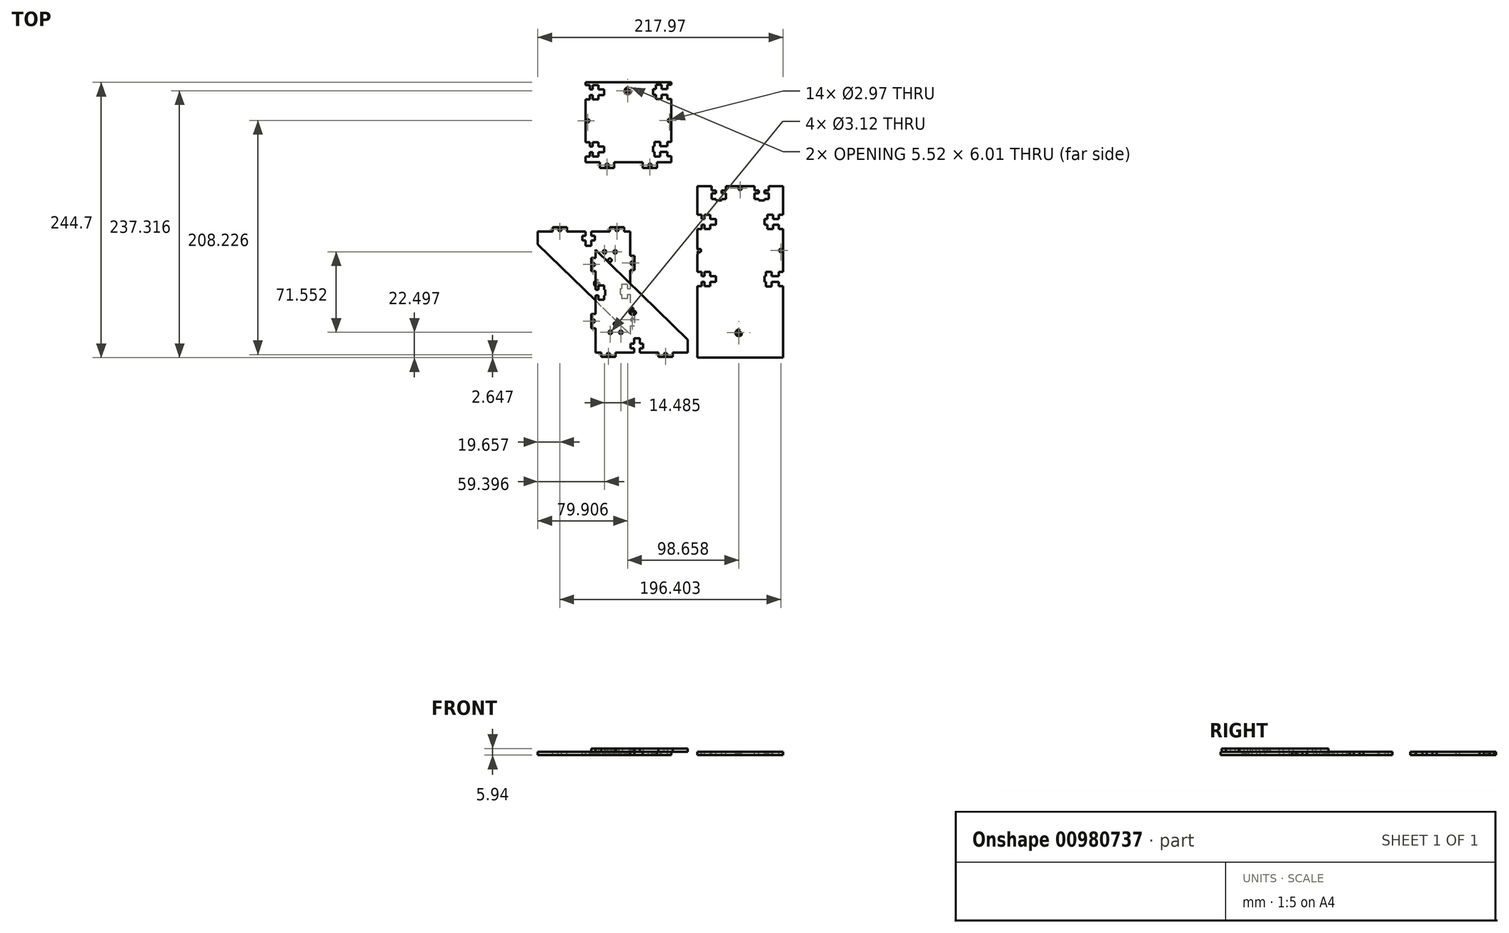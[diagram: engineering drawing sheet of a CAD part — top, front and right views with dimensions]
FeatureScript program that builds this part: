
annotation { "Feature Type Name" : "Feature", "Feature Type Description" : "" }
export const myFeature = defineFeature(function(context is Context, id is Id, definition is map)
    precondition{}
    {
        {
            var Q0;
            Q0=qCreatedBy(makeId("Top.planeOp"),FACE);
            var sketch = newSketch(context, id + "F0", { "sketchPlane" : qUnion([Q0])});
            skLineSegment(sketch, "E0.bottom", {"start": v(-31.04, 87.19) * mm, "end": v(45.16, 87.19) * mm});
            skLineSegment(sketch, "E0.top", {"start": v(-31.04, -65.21) * mm, "end": v(45.16, -65.21) * mm});
            skLineSegment(sketch, "E0.left", {"start": v(-31.04, 87.19) * mm, "end": v(-31.04, -65.21) * mm});
            skLineSegment(sketch, "E0.right", {"start": v(45.16, 87.19) * mm, "end": v(45.16, -65.21) * mm});
            skSolve(sketch);
        }
        {
            var Q0;
            Q0=qSketchRegion(id+"F0",true);
            extrude(context, id + "F1", {"entities" : qUnion([Q0]), "depth" : 2.97 * mm, "offsetDistance" : 25.4 * mm});
        }
        {
            var Q0;
            Q0=makeQuery(id+"F1.opExtrude","CAP_FACE",FACE,{"disambiguationData":[OSD([sQuery(id+"F0.wireOp",EDGE,"E0.bottom"),sQuery(id+"F0.wireOp",EDGE,"E0.top"),sQuery(id+"F0.wireOp",EDGE,"E0.left"),sQuery(id+"F0.wireOp",EDGE,"E0.right")])],"isStart":false});
            var sketch = newSketch(context, id + "F2", { "sketchPlane" : qUnion([Q0])});
            skLineSegment(sketch, "E1.bottom", {"start": v(-31.04, 61.79) * mm, "end": v(-27.23, 61.79) * mm});
            skLineSegment(sketch, "E1.top", {"start": v(-31.04, 49.09) * mm, "end": v(-27.23, 49.09) * mm});
            skLineSegment(sketch, "E1.left", {"start": v(-31.04, 61.79) * mm, "end": v(-31.04, 49.09) * mm});
            skLineSegment(sketch, "E1.right", {"start": v(-27.23, 61.79) * mm, "end": v(-27.23, 49.09) * mm});
            skLineSegment(sketch, "E2", {"start": v(-24.7, 61.79) * mm, "end": v(-24.7, 87.19) * mm, "construction": true});
            skLineSegment(sketch, "E3", {"start": v(-31.04, 33.1) * mm, "end": v(-31.04, 33.1) * mm});
            skLineSegment(sketch, "E4.bottom", {"start": v(-14.53, 52.9) * mm, "end": v(-39.93, 52.9) * mm});
            skLineSegment(sketch, "E4.top", {"start": v(-14.53, 57.98) * mm, "end": v(-39.93, 57.98) * mm});
            skLineSegment(sketch, "E4.left", {"start": v(-14.53, 52.9) * mm, "end": v(-14.53, 57.98) * mm});
            skLineSegment(sketch, "E4.right", {"start": v(-39.93, 52.9) * mm, "end": v(-39.93, 57.98) * mm});
            skPoint(sketch, "E4.middle", {"position": v(-27.23, 55.44) * mm});
            skLineSegment(sketch, "E5.bottom", {"start": v(-24.7, 61.79) * mm, "end": v(-19.61, 61.79) * mm});
            skLineSegment(sketch, "E5.top", {"start": v(-24.7, 49.09) * mm, "end": v(-19.61, 49.09) * mm});
            skLineSegment(sketch, "E5.left", {"start": v(-24.7, 61.79) * mm, "end": v(-24.7, 49.09) * mm});
            skLineSegment(sketch, "E5.right", {"start": v(-19.61, 61.79) * mm, "end": v(-19.61, 49.09) * mm});
            skLineSegment(sketch, "E6.bottom", {"start": v(-31.04, 10.99) * mm, "end": v(-27.23, 10.99) * mm});
            skLineSegment(sketch, "E6.top", {"start": v(-31.04, -1.71) * mm, "end": v(-27.23, -1.71) * mm});
            skLineSegment(sketch, "E6.left", {"start": v(-31.04, 10.99) * mm, "end": v(-31.04, -1.71) * mm});
            skLineSegment(sketch, "E6.right", {"start": v(-27.23, 10.99) * mm, "end": v(-27.23, -1.71) * mm});
            skLineSegment(sketch, "E7", {"start": v(11.23, 8.06) * mm, "end": v(11.23, 8.06) * mm});
            skLineSegment(sketch, "E8.bottom", {"start": v(-14.53, 2.1) * mm, "end": v(-39.93, 2.1) * mm});
            skLineSegment(sketch, "E8.top", {"start": v(-14.53, 7.18) * mm, "end": v(-39.93, 7.18) * mm});
            skLineSegment(sketch, "E8.left", {"start": v(-14.53, 2.1) * mm, "end": v(-14.53, 7.18) * mm});
            skLineSegment(sketch, "E8.right", {"start": v(-39.93, 2.1) * mm, "end": v(-39.93, 7.18) * mm});
            skPoint(sketch, "E8.middle", {"position": v(-27.23, 4.64) * mm});
            skLineSegment(sketch, "E9.bottom", {"start": v(-24.7, 10.99) * mm, "end": v(-19.61, 10.99) * mm});
            skLineSegment(sketch, "E9.top", {"start": v(-24.7, -1.71) * mm, "end": v(-19.61, -1.71) * mm});
            skLineSegment(sketch, "E9.left", {"start": v(-24.7, 10.99) * mm, "end": v(-24.7, -1.71) * mm});
            skLineSegment(sketch, "E9.right", {"start": v(-19.61, 10.99) * mm, "end": v(-19.61, -1.71) * mm});
            skLineSegment(sketch, "E10.bottom", {"start": v(-18.34, 87.19) * mm, "end": v(-5.64, 87.19) * mm});
            skLineSegment(sketch, "E10.top", {"start": v(-18.34, 83.38) * mm, "end": v(-5.64, 83.38) * mm});
            skLineSegment(sketch, "E10.left", {"start": v(-18.34, 87.19) * mm, "end": v(-18.34, 83.38) * mm});
            skLineSegment(sketch, "E10.right", {"start": v(-5.64, 87.19) * mm, "end": v(-5.64, 83.38) * mm});
            skLineSegment(sketch, "E11.bottom", {"start": v(19.76, 87.19) * mm, "end": v(32.46, 87.19) * mm});
            skLineSegment(sketch, "E11.top", {"start": v(19.76, 83.38) * mm, "end": v(32.46, 83.38) * mm});
            skLineSegment(sketch, "E11.left", {"start": v(19.76, 87.19) * mm, "end": v(19.76, 83.38) * mm});
            skLineSegment(sketch, "E11.right", {"start": v(32.46, 87.19) * mm, "end": v(32.46, 83.38) * mm});
            skLineSegment(sketch, "E12", {"start": v(-18.34, 85.28) * mm, "end": v(-31.04, 85.28) * mm, "construction": true});
            skLineSegment(sketch, "E13", {"start": v(32.46, 85.28) * mm, "end": v(45.16, 85.28) * mm, "construction": true});
            skLineSegment(sketch, "E14.bottom", {"start": v(-9.45, 74.49) * mm, "end": v(-14.53, 74.49) * mm});
            skLineSegment(sketch, "E14.top", {"start": v(-9.45, 99.89) * mm, "end": v(-14.53, 99.89) * mm});
            skLineSegment(sketch, "E14.left", {"start": v(-9.45, 74.49) * mm, "end": v(-9.45, 99.89) * mm});
            skLineSegment(sketch, "E14.right", {"start": v(-14.53, 74.49) * mm, "end": v(-14.53, 99.89) * mm});
            skPoint(sketch, "E14.middle", {"position": v(-12, 87.19) * mm});
            skLineSegment(sketch, "E15.bottom", {"start": v(-5.64, 80.84) * mm, "end": v(-18.34, 80.84) * mm});
            skLineSegment(sketch, "E15.top", {"start": v(-5.64, 75.76) * mm, "end": v(-18.34, 75.76) * mm});
            skLineSegment(sketch, "E15.left", {"start": v(-5.64, 80.84) * mm, "end": v(-5.64, 75.76) * mm});
            skLineSegment(sketch, "E15.right", {"start": v(-18.34, 80.84) * mm, "end": v(-18.34, 75.76) * mm});
            skLineSegment(sketch, "E16", {"start": v(-5.64, 80.84) * mm, "end": v(-5.64, 83.38) * mm, "construction": true});
            skLineSegment(sketch, "E17.bottom", {"start": v(28.65, 74.49) * mm, "end": v(23.57, 74.49) * mm});
            skLineSegment(sketch, "E17.top", {"start": v(28.65, 99.89) * mm, "end": v(23.57, 99.89) * mm});
            skLineSegment(sketch, "E17.left", {"start": v(28.65, 74.49) * mm, "end": v(28.65, 99.89) * mm});
            skLineSegment(sketch, "E17.right", {"start": v(23.57, 74.49) * mm, "end": v(23.57, 99.89) * mm});
            skPoint(sketch, "E17.middle", {"position": v(26.1, 87.19) * mm});
            skLineSegment(sketch, "E18.bottom", {"start": v(32.46, 80.84) * mm, "end": v(19.76, 80.84) * mm});
            skLineSegment(sketch, "E18.top", {"start": v(32.46, 75.76) * mm, "end": v(19.76, 75.76) * mm});
            skLineSegment(sketch, "E18.left", {"start": v(32.46, 80.84) * mm, "end": v(32.46, 75.76) * mm});
            skLineSegment(sketch, "E18.right", {"start": v(19.76, 80.84) * mm, "end": v(19.76, 75.76) * mm});
            skLineSegment(sketch, "E19", {"start": v(19.76, 80.84) * mm, "end": v(19.76, 83.38) * mm, "construction": true});
            skLineSegment(sketch, "E20", {"start": v(-29.14, 49.09) * mm, "end": v(-29.14, 10.99) * mm, "construction": true});
            skCircle(sketch, "E21", {"center": v(-29.14, 30.04) * mm, "radius": 1.49 * mm});
            skLineSegment(sketch, "E22", {"start": v(-5.64, 85.28) * mm, "end": v(19.76, 85.28) * mm, "construction": true});
            skCircle(sketch, "E23", {"center": v(7.06, 85.28) * mm, "radius": 1.49 * mm});
            skLineSegment(sketch, "E24", {"start": v(-27.23, 49.09) * mm, "end": v(-24.7, 49.09) * mm, "construction": true});
            skLineSegment(sketch, "E25.bottom", {"start": v(45.16, 61.79) * mm, "end": v(41.35, 61.79) * mm});
            skLineSegment(sketch, "E25.top", {"start": v(45.16, 49.09) * mm, "end": v(41.35, 49.09) * mm});
            skLineSegment(sketch, "E25.left", {"start": v(45.16, 61.79) * mm, "end": v(45.16, 49.09) * mm});
            skLineSegment(sketch, "E25.right", {"start": v(41.35, 61.79) * mm, "end": v(41.35, 49.09) * mm});
            skLineSegment(sketch, "E26", {"start": v(41.35, 61.79) * mm, "end": v(41.35, 87.19) * mm, "construction": true});
            skLineSegment(sketch, "E27.bottom", {"start": v(28.65, 57.98) * mm, "end": v(54.05, 57.98) * mm});
            skLineSegment(sketch, "E27.top", {"start": v(28.65, 52.9) * mm, "end": v(54.05, 52.9) * mm});
            skLineSegment(sketch, "E27.left", {"start": v(28.65, 57.98) * mm, "end": v(28.65, 52.9) * mm});
            skLineSegment(sketch, "E27.right", {"start": v(54.05, 57.98) * mm, "end": v(54.05, 52.9) * mm});
            skPoint(sketch, "E27.middle", {"position": v(41.35, 55.44) * mm});
            skLineSegment(sketch, "E28.bottom", {"start": v(36.27, 61.79) * mm, "end": v(31.19, 61.79) * mm});
            skLineSegment(sketch, "E28.top", {"start": v(36.27, 49.09) * mm, "end": v(31.19, 49.09) * mm});
            skLineSegment(sketch, "E28.left", {"start": v(36.27, 61.79) * mm, "end": v(36.27, 49.09) * mm});
            skLineSegment(sketch, "E28.right", {"start": v(31.19, 61.79) * mm, "end": v(31.19, 49.09) * mm});
            skLineSegment(sketch, "E29", {"start": v(36.27, 49.09) * mm, "end": v(41.35, 49.09) * mm, "construction": true});
            skLineSegment(sketch, "E30.bottom", {"start": v(45.16, 10.99) * mm, "end": v(41.35, 10.99) * mm});
            skLineSegment(sketch, "E30.top", {"start": v(45.16, -1.71) * mm, "end": v(41.35, -1.71) * mm});
            skLineSegment(sketch, "E30.left", {"start": v(45.16, 10.99) * mm, "end": v(45.16, -1.71) * mm});
            skLineSegment(sketch, "E30.right", {"start": v(41.35, 10.99) * mm, "end": v(41.35, -1.71) * mm});
            skLineSegment(sketch, "E31.bottom", {"start": v(28.65, 7.18) * mm, "end": v(54.05, 7.18) * mm});
            skLineSegment(sketch, "E31.top", {"start": v(28.65, 2.1) * mm, "end": v(54.05, 2.1) * mm});
            skLineSegment(sketch, "E31.left", {"start": v(28.65, 7.18) * mm, "end": v(28.65, 2.1) * mm});
            skLineSegment(sketch, "E31.right", {"start": v(54.05, 7.18) * mm, "end": v(54.05, 2.1) * mm});
            skPoint(sketch, "E31.middle", {"position": v(41.35, 4.64) * mm});
            skLineSegment(sketch, "E32.bottom", {"start": v(34.98, 10.99) * mm, "end": v(30.02, 10.99) * mm});
            skLineSegment(sketch, "E32.top", {"start": v(34.98, -2) * mm, "end": v(30.02, -2) * mm});
            skLineSegment(sketch, "E32.left", {"start": v(34.98, 10.99) * mm, "end": v(34.98, -2) * mm});
            skLineSegment(sketch, "E32.right", {"start": v(30.02, 10.99) * mm, "end": v(30.02, -2) * mm});
            skLineSegment(sketch, "E33", {"start": v(41.35, 49.09) * mm, "end": v(43.25, 49.09) * mm, "construction": true});
            skLineSegment(sketch, "E34", {"start": v(43.25, 10.99) * mm, "end": v(43.25, 49.09) * mm, "construction": true});
            skCircle(sketch, "E35", {"center": v(43.25, 30.04) * mm, "radius": 1.49 * mm});
            skSolve(sketch);
        }
        {
            var Q0;
            Q0=qSketchRegion(id+"F2",true);
            extrude(context, id + "F3", {"entities" : qUnion([Q0]), "operationType" : NewBodyOperationType.REMOVE, "oppositeDirection" : true, "depth" : 25.4 * mm, "offsetDistance" : 25.4 * mm});
        }
        {
            var Q0;
            Q0=qCreatedBy(makeId("Top.planeOp"),FACE);
            var sketch = newSketch(context, id + "F4", { "sketchPlane" : qUnion([Q0])});
            skLineSegment(sketch, "E36.bottom", {"start": v(-43.25, 86.15) * mm, "end": v(-129.12, 86.15) * mm});
            skLineSegment(sketch, "E36.top", {"start": v(-43.25, -66.25) * mm, "end": v(-129.12, -66.25) * mm});
            skLineSegment(sketch, "E36.left", {"start": v(-43.25, 86.15) * mm, "end": v(-43.25, -66.25) * mm});
            skLineSegment(sketch, "E36.right", {"start": v(-129.12, 86.15) * mm, "end": v(-129.12, -66.25) * mm});
            skSolve(sketch);
        }
        {
            var Q0;
            Q0=qSketchRegion(id+"F4",true);
            extrude(context, id + "F5", {"entities" : qUnion([Q0]), "depth" : 2.97 * mm, "offsetDistance" : 25.4 * mm});
        }
        {
            var Q0;
            Q0=makeQuery(id+"F5.opExtrude","CAP_FACE",FACE,{"disambiguationData":[OSD([sQuery(id+"F4.wireOp",EDGE,"E36.bottom"),sQuery(id+"F4.wireOp",EDGE,"E36.top"),sQuery(id+"F4.wireOp",EDGE,"E36.left"),sQuery(id+"F4.wireOp",EDGE,"E36.right")])],"isStart":false});
            var sketch = newSketch(context, id + "F6", { "sketchPlane" : qUnion([Q0])});
            skLineSegment(sketch, "E37.bottom", {"start": v(-43.25, 86.15) * mm, "end": v(-47.06, 86.15) * mm});
            skLineSegment(sketch, "E37.top", {"start": v(-43.25, 60.75) * mm, "end": v(-47.06, 60.75) * mm});
            skLineSegment(sketch, "E37.left", {"start": v(-43.25, 86.15) * mm, "end": v(-43.25, 60.75) * mm});
            skLineSegment(sketch, "E37.right", {"start": v(-47.06, 86.15) * mm, "end": v(-47.06, 60.75) * mm});
            skLineSegment(sketch, "E38", {"start": v(-46.12, 86.15) * mm, "end": v(-46.12, 86.15) * mm});
            skLineSegment(sketch, "E39", {"start": v(-43.25, 68.93) * mm, "end": v(-43.25, 68.93) * mm});
            skLineSegment(sketch, "E40.bottom", {"start": v(-43.25, 48.05) * mm, "end": v(-47.06, 48.05) * mm});
            skLineSegment(sketch, "E40.top", {"start": v(-43.25, 9.95) * mm, "end": v(-47.06, 9.95) * mm});
            skLineSegment(sketch, "E40.left", {"start": v(-43.25, 48.05) * mm, "end": v(-43.25, 9.95) * mm});
            skLineSegment(sketch, "E40.right", {"start": v(-47.06, 48.05) * mm, "end": v(-47.06, 9.95) * mm});
            skLineSegment(sketch, "E41", {"start": v(-45.15, 60.75) * mm, "end": v(-45.15, 48.05) * mm, "construction": true});
            skLineSegment(sketch, "E42.bottom", {"start": v(-43.25, -1.8) * mm, "end": v(-47.06, -1.8) * mm});
            skLineSegment(sketch, "E42.top", {"start": v(-43.25, -174.53) * mm, "end": v(-47.06, -174.53) * mm});
            skLineSegment(sketch, "E42.left", {"start": v(-43.25, -1.8) * mm, "end": v(-43.25, -174.53) * mm});
            skLineSegment(sketch, "E42.right", {"start": v(-47.06, -1.8) * mm, "end": v(-47.06, -174.53) * mm});
            skLineSegment(sketch, "E43.bottom", {"start": v(-43.25, 35.35) * mm, "end": v(-47.06, 35.35) * mm});
            skLineSegment(sketch, "E43.top", {"start": v(-43.25, 22.65) * mm, "end": v(-47.06, 22.65) * mm});
            skLineSegment(sketch, "E43.left", {"start": v(-43.25, 35.35) * mm, "end": v(-43.25, 22.65) * mm});
            skLineSegment(sketch, "E43.right", {"start": v(-47.06, 35.35) * mm, "end": v(-47.06, 22.65) * mm});
            skLineSegment(sketch, "E44", {"start": v(-45.15, 48.05) * mm, "end": v(-45.15, 35.35) * mm, "construction": true});
            skLineSegment(sketch, "E45", {"start": v(-45.15, 9.95) * mm, "end": v(-45.15, 22.65) * mm, "construction": true});
            skLineSegment(sketch, "E46.bottom", {"start": v(-55.95, 31.54) * mm, "end": v(-30.55, 31.54) * mm});
            skLineSegment(sketch, "E46.top", {"start": v(-55.95, 26.46) * mm, "end": v(-30.55, 26.46) * mm});
            skLineSegment(sketch, "E46.left", {"start": v(-55.95, 31.54) * mm, "end": v(-55.95, 26.46) * mm});
            skLineSegment(sketch, "E46.right", {"start": v(-30.55, 31.54) * mm, "end": v(-30.55, 26.46) * mm});
            skPoint(sketch, "E46.middle", {"position": v(-43.25, 29) * mm});
            skLineSegment(sketch, "E47.bottom", {"start": v(-49.6, 35.35) * mm, "end": v(-54.68, 35.35) * mm});
            skLineSegment(sketch, "E47.top", {"start": v(-49.6, 22.65) * mm, "end": v(-54.68, 22.65) * mm});
            skLineSegment(sketch, "E47.left", {"start": v(-49.6, 35.35) * mm, "end": v(-49.6, 22.65) * mm});
            skLineSegment(sketch, "E47.right", {"start": v(-54.68, 35.35) * mm, "end": v(-54.68, 22.65) * mm});
            skLineSegment(sketch, "E48", {"start": v(-49.6, 33.67) * mm, "end": v(-47.06, 33.67) * mm, "construction": true});
            skCircle(sketch, "E49", {"center": v(-45.15, 54.4) * mm, "radius": 1.49 * mm});
            skLineSegment(sketch, "E50", {"start": v(-45.15, 9.95) * mm, "end": v(-45.15, -1.8) * mm, "construction": true});
            skCircle(sketch, "E51", {"center": v(-45.15, 4.08) * mm, "radius": 1.49 * mm});
            skLineSegment(sketch, "E52.bottom", {"start": v(-47.06, 82.34) * mm, "end": v(-52.31, 82.34) * mm});
            skLineSegment(sketch, "E52.top", {"start": v(-47.06, 86.15) * mm, "end": v(-52.31, 86.15) * mm});
            skLineSegment(sketch, "E52.left", {"start": v(-47.06, 82.34) * mm, "end": v(-47.06, 86.15) * mm});
            skLineSegment(sketch, "E52.right", {"start": v(-52.31, 82.34) * mm, "end": v(-52.31, 86.15) * mm});
            skLineSegment(sketch, "E53", {"start": v(-52.31, 82.34) * mm, "end": v(-65.01, 82.34) * mm, "construction": true});
            skLineSegment(sketch, "E54.bottom", {"start": v(-65.01, 82.34) * mm, "end": v(-103.11, 82.34) * mm});
            skLineSegment(sketch, "E54.top", {"start": v(-65.01, 86.15) * mm, "end": v(-103.11, 86.15) * mm});
            skLineSegment(sketch, "E54.left", {"start": v(-65.01, 82.34) * mm, "end": v(-65.01, 86.15) * mm});
            skLineSegment(sketch, "E54.right", {"start": v(-103.11, 82.34) * mm, "end": v(-103.11, 86.15) * mm});
            skLineSegment(sketch, "E55", {"start": v(-103.11, 82.34) * mm, "end": v(-115.81, 82.34) * mm, "construction": true});
            skLineSegment(sketch, "E56.bottom", {"start": v(-115.81, 82.34) * mm, "end": v(-130.63, 82.34) * mm});
            skLineSegment(sketch, "E56.top", {"start": v(-115.81, 87.7) * mm, "end": v(-130.63, 87.7) * mm});
            skLineSegment(sketch, "E56.left", {"start": v(-115.81, 82.34) * mm, "end": v(-115.81, 87.7) * mm});
            skLineSegment(sketch, "E56.right", {"start": v(-130.63, 82.34) * mm, "end": v(-130.63, 87.7) * mm});
            skLineSegment(sketch, "E57", {"start": v(-103.11, 84.25) * mm, "end": v(-115.81, 84.25) * mm, "construction": true});
            skCircle(sketch, "E58", {"center": v(-109.46, 84.25) * mm, "radius": 1.49 * mm});
            skLineSegment(sketch, "E59", {"start": v(-65.01, 84.25) * mm, "end": v(-52.31, 84.25) * mm, "construction": true});
            skCircle(sketch, "E60", {"center": v(-58.66, 84.25) * mm, "radius": 1.49 * mm});
            skLineSegment(sketch, "E61.bottom", {"start": v(-86.6, 69.64) * mm, "end": v(-81.52, 69.64) * mm});
            skLineSegment(sketch, "E61.top", {"start": v(-86.6, 95.04) * mm, "end": v(-81.52, 95.04) * mm});
            skLineSegment(sketch, "E61.left", {"start": v(-86.6, 69.64) * mm, "end": v(-86.6, 95.04) * mm});
            skLineSegment(sketch, "E61.right", {"start": v(-81.52, 69.64) * mm, "end": v(-81.52, 95.04) * mm});
            skPoint(sketch, "E61.middle", {"position": v(-84.06, 82.34) * mm});
            skLineSegment(sketch, "E62.bottom", {"start": v(-89.43, 78.63) * mm, "end": v(-78.4, 78.63) * mm});
            skLineSegment(sketch, "E62.top", {"start": v(-89.43, 74.47) * mm, "end": v(-78.4, 74.47) * mm});
            skLineSegment(sketch, "E62.left", {"start": v(-89.43, 78.63) * mm, "end": v(-89.43, 74.47) * mm});
            skLineSegment(sketch, "E62.right", {"start": v(-78.4, 78.63) * mm, "end": v(-78.4, 74.47) * mm});
            skSolve(sketch);
        }
        {
            var Q0;
            Q0=qSketchRegion(id+"F6",true);
            extrude(context, id + "F7", {"entities" : qUnion([Q0]), "operationType" : NewBodyOperationType.REMOVE, "oppositeDirection" : true, "depth" : 25.4 * mm, "offsetDistance" : 25.4 * mm});
        }
        {
            var Q0;
            Q0=qCreatedBy(makeId("Top.planeOp"),FACE);
            var sketch = newSketch(context, id + "F8", { "sketchPlane" : qUnion([Q0])});
            skLineSegment(sketch, "E63.bottom", {"start": v(-30.12, 88.56) * mm, "end": v(46.08, 88.56) * mm});
            skLineSegment(sketch, "E63.top", {"start": v(-30.12, 164.76) * mm, "end": v(46.08, 164.76) * mm});
            skLineSegment(sketch, "E63.left", {"start": v(-30.12, 88.56) * mm, "end": v(-30.12, 164.76) * mm});
            skLineSegment(sketch, "E63.right", {"start": v(46.08, 88.56) * mm, "end": v(46.08, 164.76) * mm});
            skSolve(sketch);
        }
        {
            var Q0;
            Q0=qSketchRegion(id+"F8",true);
            extrude(context, id + "F9", {"entities" : qUnion([Q0]), "depth" : 2.97 * mm, "offsetDistance" : 25.4 * mm});
        }
        {
            var Q0;
            Q0=makeQuery(id+"F9.opExtrude","CAP_FACE",FACE,{"disambiguationData":[OSD([sQuery(id+"F8.wireOp",EDGE,"E63.bottom"),sQuery(id+"F8.wireOp",EDGE,"E63.top"),sQuery(id+"F8.wireOp",EDGE,"E63.left"),sQuery(id+"F8.wireOp",EDGE,"E63.right")])],"isStart":false});
            var sketch = newSketch(context, id + "F10", { "sketchPlane" : qUnion([Q0])});
            skLineSegment(sketch, "E64.bottom", {"start": v(-30.12, 93.64) * mm, "end": v(-17.42, 93.64) * mm});
            skLineSegment(sketch, "E64.top", {"start": v(-30.12, 88.56) * mm, "end": v(-17.42, 88.56) * mm});
            skLineSegment(sketch, "E64.left", {"start": v(-30.12, 93.64) * mm, "end": v(-30.12, 88.56) * mm});
            skLineSegment(sketch, "E64.right", {"start": v(-17.42, 93.64) * mm, "end": v(-17.42, 88.56) * mm});
            skLineSegment(sketch, "E65.bottom", {"start": v(-4.72, 93.64) * mm, "end": v(20.68, 93.64) * mm});
            skLineSegment(sketch, "E65.top", {"start": v(-4.72, 88.56) * mm, "end": v(20.68, 88.56) * mm});
            skLineSegment(sketch, "E65.left", {"start": v(-4.72, 93.64) * mm, "end": v(-4.72, 88.56) * mm});
            skLineSegment(sketch, "E65.right", {"start": v(20.68, 93.64) * mm, "end": v(20.68, 88.56) * mm});
            skLineSegment(sketch, "E66", {"start": v(-17.42, 91.1) * mm, "end": v(-4.72, 91.1) * mm, "construction": true});
            skCircle(sketch, "E67", {"center": v(-11.07, 91.1) * mm, "radius": 1.49 * mm});
            skLineSegment(sketch, "E68.bottom", {"start": v(46.08, 88.56) * mm, "end": v(33.38, 88.56) * mm});
            skLineSegment(sketch, "E68.top", {"start": v(46.08, 93.65) * mm, "end": v(33.38, 93.65) * mm});
            skLineSegment(sketch, "E68.left", {"start": v(46.08, 88.56) * mm, "end": v(46.08, 93.65) * mm});
            skLineSegment(sketch, "E68.right", {"start": v(33.38, 88.56) * mm, "end": v(33.38, 93.65) * mm});
            skLineSegment(sketch, "E69", {"start": v(20.68, 91.1) * mm, "end": v(33.38, 91.1) * mm, "construction": true});
            skCircle(sketch, "E70", {"center": v(27.03, 91.1) * mm, "radius": 1.49 * mm});
            skLineSegment(sketch, "E71.bottom", {"start": v(-30.23, 162.4) * mm, "end": v(-26.42, 162.4) * mm});
            skLineSegment(sketch, "E71.top", {"start": v(-30.23, 149.7) * mm, "end": v(-26.42, 149.7) * mm});
            skLineSegment(sketch, "E71.left", {"start": v(-30.23, 162.4) * mm, "end": v(-30.23, 149.7) * mm});
            skLineSegment(sketch, "E71.right", {"start": v(-26.42, 162.4) * mm, "end": v(-26.42, 149.7) * mm});
            skLineSegment(sketch, "E72", {"start": v(-23.88, 162.4) * mm, "end": v(-23.88, 187.8) * mm, "construction": true});
            skLineSegment(sketch, "E73", {"start": v(27.43, 133.71) * mm, "end": v(27.43, 133.71) * mm});
            skLineSegment(sketch, "E74.bottom", {"start": v(-13.72, 153.5) * mm, "end": v(-39.12, 153.5) * mm});
            skLineSegment(sketch, "E74.top", {"start": v(-13.72, 158.59) * mm, "end": v(-39.12, 158.59) * mm});
            skLineSegment(sketch, "E74.left", {"start": v(-13.72, 153.5) * mm, "end": v(-13.72, 158.59) * mm});
            skLineSegment(sketch, "E74.right", {"start": v(-39.12, 153.5) * mm, "end": v(-39.12, 158.59) * mm});
            skPoint(sketch, "E74.middle", {"position": v(-26.42, 156.05) * mm});
            skLineSegment(sketch, "E75.bottom", {"start": v(-23.88, 162.4) * mm, "end": v(-18.8, 162.4) * mm});
            skLineSegment(sketch, "E75.top", {"start": v(-23.88, 149.7) * mm, "end": v(-18.8, 149.7) * mm});
            skLineSegment(sketch, "E75.left", {"start": v(-23.88, 162.4) * mm, "end": v(-23.88, 149.7) * mm});
            skLineSegment(sketch, "E75.right", {"start": v(-18.8, 162.4) * mm, "end": v(-18.8, 149.7) * mm});
            skLineSegment(sketch, "E76.bottom", {"start": v(-30.23, 111.6) * mm, "end": v(-26.42, 111.6) * mm});
            skLineSegment(sketch, "E76.top", {"start": v(-30.23, 98.9) * mm, "end": v(-26.42, 98.9) * mm});
            skLineSegment(sketch, "E76.left", {"start": v(-30.23, 111.6) * mm, "end": v(-30.23, 98.9) * mm});
            skLineSegment(sketch, "E76.right", {"start": v(-26.42, 111.6) * mm, "end": v(-26.42, 98.9) * mm});
            skLineSegment(sketch, "E77.bottom", {"start": v(-13.72, 102.7) * mm, "end": v(-39.12, 102.7) * mm});
            skLineSegment(sketch, "E77.top", {"start": v(-13.72, 107.79) * mm, "end": v(-39.12, 107.79) * mm});
            skLineSegment(sketch, "E77.left", {"start": v(-13.72, 102.7) * mm, "end": v(-13.72, 107.79) * mm});
            skLineSegment(sketch, "E77.right", {"start": v(-39.12, 102.7) * mm, "end": v(-39.12, 107.79) * mm});
            skPoint(sketch, "E77.middle", {"position": v(-26.42, 105.25) * mm});
            skLineSegment(sketch, "E78.bottom", {"start": v(-23.88, 111.6) * mm, "end": v(-18.8, 111.6) * mm});
            skLineSegment(sketch, "E78.top", {"start": v(-23.88, 98.9) * mm, "end": v(-18.8, 98.9) * mm});
            skLineSegment(sketch, "E78.left", {"start": v(-23.88, 111.6) * mm, "end": v(-23.88, 98.9) * mm});
            skLineSegment(sketch, "E78.right", {"start": v(-18.8, 111.6) * mm, "end": v(-18.8, 98.9) * mm});
            skLineSegment(sketch, "E79", {"start": v(-28.32, 149.7) * mm, "end": v(-28.32, 111.6) * mm, "construction": true});
            skCircle(sketch, "E80", {"center": v(-28.32, 130.65) * mm, "radius": 1.49 * mm});
            skLineSegment(sketch, "E81", {"start": v(-26.42, 149.7) * mm, "end": v(-23.88, 149.7) * mm, "construction": true});
            skLineSegment(sketch, "E82.bottom", {"start": v(46.27, 162.68) * mm, "end": v(42.46, 162.68) * mm});
            skLineSegment(sketch, "E82.top", {"start": v(46.27, 149.98) * mm, "end": v(42.46, 149.98) * mm});
            skLineSegment(sketch, "E82.left", {"start": v(46.27, 162.68) * mm, "end": v(46.27, 149.98) * mm});
            skLineSegment(sketch, "E82.right", {"start": v(42.46, 162.68) * mm, "end": v(42.46, 149.98) * mm});
            skLineSegment(sketch, "E83.bottom", {"start": v(29.76, 158.87) * mm, "end": v(55.16, 158.87) * mm});
            skLineSegment(sketch, "E83.top", {"start": v(29.76, 153.8) * mm, "end": v(55.16, 153.8) * mm});
            skLineSegment(sketch, "E83.left", {"start": v(29.76, 158.87) * mm, "end": v(29.76, 153.8) * mm});
            skLineSegment(sketch, "E83.right", {"start": v(55.16, 158.87) * mm, "end": v(55.16, 153.8) * mm});
            skPoint(sketch, "E83.middle", {"position": v(42.46, 156.33) * mm});
            skLineSegment(sketch, "E84.bottom", {"start": v(37.38, 162.68) * mm, "end": v(32.3, 162.68) * mm});
            skLineSegment(sketch, "E84.top", {"start": v(37.38, 149.98) * mm, "end": v(32.3, 149.98) * mm});
            skLineSegment(sketch, "E84.left", {"start": v(37.38, 162.68) * mm, "end": v(37.38, 149.98) * mm});
            skLineSegment(sketch, "E84.right", {"start": v(32.3, 162.68) * mm, "end": v(32.3, 149.98) * mm});
            skLineSegment(sketch, "E85", {"start": v(37.38, 149.98) * mm, "end": v(42.46, 149.98) * mm, "construction": true});
            skLineSegment(sketch, "E86.bottom", {"start": v(46.27, 111.88) * mm, "end": v(42.46, 111.88) * mm});
            skLineSegment(sketch, "E86.top", {"start": v(46.27, 99.18) * mm, "end": v(42.46, 99.18) * mm});
            skLineSegment(sketch, "E86.left", {"start": v(46.27, 111.88) * mm, "end": v(46.27, 99.18) * mm});
            skLineSegment(sketch, "E86.right", {"start": v(42.46, 111.88) * mm, "end": v(42.46, 99.18) * mm});
            skLineSegment(sketch, "E87.bottom", {"start": v(29.76, 108.07) * mm, "end": v(55.16, 108.07) * mm});
            skLineSegment(sketch, "E87.top", {"start": v(29.76, 103) * mm, "end": v(55.16, 103) * mm});
            skLineSegment(sketch, "E87.left", {"start": v(29.76, 108.07) * mm, "end": v(29.76, 103) * mm});
            skLineSegment(sketch, "E87.right", {"start": v(55.16, 108.07) * mm, "end": v(55.16, 103) * mm});
            skPoint(sketch, "E87.middle", {"position": v(42.46, 105.53) * mm});
            skLineSegment(sketch, "E88.bottom", {"start": v(36.1, 111.88) * mm, "end": v(31.14, 111.88) * mm});
            skLineSegment(sketch, "E88.top", {"start": v(36.1, 98.9) * mm, "end": v(31.14, 98.9) * mm});
            skLineSegment(sketch, "E88.left", {"start": v(36.1, 111.88) * mm, "end": v(36.1, 98.9) * mm});
            skLineSegment(sketch, "E88.right", {"start": v(31.14, 111.88) * mm, "end": v(31.14, 98.9) * mm});
            skLineSegment(sketch, "E89", {"start": v(42.46, 149.98) * mm, "end": v(44.37, 149.98) * mm, "construction": true});
            skLineSegment(sketch, "E90", {"start": v(44.37, 111.88) * mm, "end": v(44.37, 149.98) * mm, "construction": true});
            skCircle(sketch, "E91", {"center": v(44.37, 130.93) * mm, "radius": 1.49 * mm});
            skLineSegment(sketch, "E92", {"start": v(-28.32, 98.9) * mm, "end": v(-28.32, 88.56) * mm, "construction": true});
            skLineSegment(sketch, "E93", {"start": v(44.37, 98.9) * mm, "end": v(44.37, 88.56) * mm});
            skPoint(sketch, "E93.startSnap0", {"position": v(44.37, 99.18) * mm});
            skLineSegment(sketch, "E94", {"start": v(-21.34, 98.9) * mm, "end": v(-21.34, 93.64) * mm, "construction": true});
            skSolve(sketch);
        }
        {
            var Q0;
            Q0=qSketchRegion(id+"F10",true);
            extrude(context, id + "F11", {"entities" : qUnion([Q0]), "operationType" : NewBodyOperationType.REMOVE, "oppositeDirection" : true, "depth" : 25.4 * mm, "offsetDistance" : 25.4 * mm});
        }
        {
            var Q0;
            Q0=makeQuery(id+"F5.opExtrude","CAP_FACE",FACE,{"disambiguationData":[OSD([sQuery(id+"F4.wireOp",EDGE,"E36.bottom"),sQuery(id+"F4.wireOp",EDGE,"E36.top"),sQuery(id+"F4.wireOp",EDGE,"E36.left"),sQuery(id+"F4.wireOp",EDGE,"E36.right")])],"isStart":false});
            var sketch = newSketch(context, id + "F12", { "sketchPlane" : qUnion([Q0])});
            skLineSegment(sketch, "E95", {"start": v(-131.6, 73.32) * mm, "end": v(-43.21, -12.62) * mm});
            skLineSegment(sketch, "E96", {"start": v(-43.21, -12.62) * mm, "end": v(-43.21, -72.98) * mm});
            skLineSegment(sketch, "E97", {"start": v(-43.21, -72.98) * mm, "end": v(-145.1, -72.6) * mm});
            skLineSegment(sketch, "E98", {"start": v(-145.1, -72.6) * mm, "end": v(-131.46, 73.72) * mm});
            skSolve(sketch);
        }
        {
            var Q0;
            Q0=qSketchRegion(id+"F12",true);
            extrude(context, id + "F13", {"entities" : qUnion([Q0]), "operationType" : NewBodyOperationType.REMOVE, "oppositeDirection" : true, "depth" : 25.4 * mm, "offsetDistance" : 25.4 * mm});
        }
        {
            var Q0;
            Q0=qCreatedBy(makeId("Right.planeOp"),FACE);
            cPlane(context, id + "F14", {"entities" : qUnion([Q0]), "cplaneType" : CPlaneType.OFFSET, "offset" : 25.4 * mm, "width" : 152.4 * mm, "height" : 152.4 * mm});
        }
        {
            var Q0;
            Q0=makeQuery(id+"F5.opExtrude","SWEPT_BODY",BODY,{"disambiguationData":[OSD([sQuery(id+"F4.wireOp",EDGE,"E36.bottom"),sQuery(id+"F4.wireOp",EDGE,"E36.top"),sQuery(id+"F4.wireOp",EDGE,"E36.left"),sQuery(id+"F4.wireOp",EDGE,"E36.right")])]});
            var Q1;
            Q1=qCreatedBy(id+"F14.planeOp",FACE);
            mirror(context, id + "F15", {"entities" : qUnion([Q0]), "mirrorPlane" : qUnion([Q1])});
        }
        {
            var Q0;
            Q0=makeQuery(id+"F15.opPattern","COPY",BODY,{"derivedFrom":makeQuery(id+"F5.opExtrude","SWEPT_BODY",BODY,{"disambiguationData":[OSD([sQuery(id+"F4.wireOp",EDGE,"E36.bottom"),sQuery(id+"F4.wireOp",EDGE,"E36.top"),sQuery(id+"F4.wireOp",EDGE,"E36.left"),sQuery(id+"F4.wireOp",EDGE,"E36.right")])]}),"instanceName":"1"});
            transform(context, id + "F16", {"entities" : qUnion([Q0]), "transformType" : TransformType.TRANSLATION_3D, "dx" : -226.57 * mm, "dy" : -115.06 * mm, "dz" : 0 * mm, "makeCopy" : false});
        }
        {
            var Q0;
            Q0=makeQuery(id+"F15.opPattern","COPY",BODY,{"derivedFrom":makeQuery(id+"F5.opExtrude","SWEPT_BODY",BODY,{"disambiguationData":[OSD([sQuery(id+"F4.wireOp",EDGE,"E36.bottom"),sQuery(id+"F4.wireOp",EDGE,"E36.top"),sQuery(id+"F4.wireOp",EDGE,"E36.left"),sQuery(id+"F4.wireOp",EDGE,"E36.right")])]}),"instanceName":"1"});
            var Q1;
            {var subQ0=sQuery(id+"F4.wireOp",EDGE,"E36.bottom");Q1=makeQuery(id+"F15.opPattern","COPY",EDGE,{"derivedFrom":makeQuery(id+"F7.boolean.opBoolean","SPLIT",EDGE,{"disambiguationData":[TD([makeQuery(id+"F7.opExtrude","SWEPT_FACE",FACE,{"disambiguationData":[OSD([sQuery(id+"F6.wireOp",EDGE,"E52.right")])]})])],"derivedFrom":makeQuery(id+"F5.opExtrude","CAP_EDGE",EDGE,{"disambiguationData":[OSD([subQ0])],"isStart":false})}),"instanceName":"1"});}
            transform(context, id + "F17", {"entities" : qUnion([Q0]), "transformType" : TransformType.ROTATION, "transformAxis" : qUnion([Q1]), "angle" : 180 * degree, "makeCopy" : false});
        }
        {
            var Q0;
            Q0=makeQuery(id+"F5.opExtrude","SWEPT_BODY",BODY,{"disambiguationData":[OSD([sQuery(id+"F4.wireOp",EDGE,"E36.bottom"),sQuery(id+"F4.wireOp",EDGE,"E36.top"),sQuery(id+"F4.wireOp",EDGE,"E36.left"),sQuery(id+"F4.wireOp",EDGE,"E36.right")])]});
            var Q1;
            Q1=makeQuery(id+"F15.opPattern","COPY",BODY,{"derivedFrom":makeQuery(id+"F5.opExtrude","SWEPT_BODY",BODY,{"disambiguationData":[OSD([sQuery(id+"F4.wireOp",EDGE,"E36.bottom"),sQuery(id+"F4.wireOp",EDGE,"E36.top"),sQuery(id+"F4.wireOp",EDGE,"E36.left"),sQuery(id+"F4.wireOp",EDGE,"E36.right")])]}),"instanceName":"1"});
            transform(context, id + "F18", {"entities" : qUnion([Q0, Q1]), "transformType" : TransformType.TRANSLATION_3D, "dx" : 7.11 * mm, "dy" : -35.56 * mm, "dz" : 0 * mm, "makeCopy" : false});
        }
        {
            var Q0;
            Q0=makeQuery(id+"F9.opExtrude","SWEPT_BODY",BODY,{"disambiguationData":[OSD([sQuery(id+"F8.wireOp",EDGE,"E63.bottom"),sQuery(id+"F8.wireOp",EDGE,"E63.top"),sQuery(id+"F8.wireOp",EDGE,"E63.left"),sQuery(id+"F8.wireOp",EDGE,"E63.right")])]});
            transform(context, id + "F19", {"entities" : qUnion([Q0]), "transformType" : TransformType.TRANSLATION_3D, "dx" : -87.38 * mm, "dy" : -36.07 * mm, "dz" : 0 * mm, "makeCopy" : false});
        }
        {
            var Q0;
            Q0=makeQuery(id+"F1.opExtrude","CAP_FACE",FACE,{"disambiguationData":[OSD([sQuery(id+"F0.wireOp",EDGE,"E0.bottom"),sQuery(id+"F0.wireOp",EDGE,"E0.top"),sQuery(id+"F0.wireOp",EDGE,"E0.left"),sQuery(id+"F0.wireOp",EDGE,"E0.right")])],"isStart":false});
            var sketch = newSketch(context, id + "F20", { "sketchPlane" : qUnion([Q0])});
            skArc(sketch, "E99", {"start": v(6.45, -40.06) * mm, "mid": v(3.55, -41.54) * mm, "end": v(3.28, -44.78) * mm});
            skArc(sketch, "E100", {"start": v(3.28, -44.78) * mm, "mid": v(5.88, -46.07) * mm, "end": v(8.48, -44.78) * mm});
            skArc(sketch, "E101", {"start": v(8.48, -44.78) * mm, "mid": v(7.45, -42.5) * mm, "end": v(4.97, -42.81) * mm});
            skArc(sketch, "E102", {"start": v(6.42, -40.72) * mm, "mid": v(3.76, -43.87) * mm, "end": v(7.78, -44.78) * mm});
            skArc(sketch, "E103", {"start": v(7.78, -44.78) * mm, "mid": v(6.95, -43.24) * mm, "end": v(5.23, -43.56) * mm});
            skLineSegment(sketch, "E104", {"start": v(6.45, -40.06) * mm, "end": v(6.42, -40.72) * mm});
            skLineSegment(sketch, "E105", {"start": v(4.97, -42.81) * mm, "end": v(5.23, -43.56) * mm});
            skSolve(sketch);
        }
        {
            var Q0;
            Q0=qSketchRegion(id+"F20",true);
            extrude(context, id + "F21", {"entities" : qUnion([Q0]), "operationType" : NewBodyOperationType.REMOVE, "oppositeDirection" : true, "depth" : 25.4 * mm, "offsetDistance" : 25.4 * mm});
        }
        {
            var Q0;
            Q0=makeQuery(id+"F9.opExtrude","CAP_FACE",FACE,{"disambiguationData":[OSD([sQuery(id+"F8.wireOp",EDGE,"E63.bottom"),sQuery(id+"F8.wireOp",EDGE,"E63.top"),sQuery(id+"F8.wireOp",EDGE,"E63.left"),sQuery(id+"F8.wireOp",EDGE,"E63.right")])],"isStart":false});
            var sketch = newSketch(context, id + "F22", { "sketchPlane" : qUnion([Q0])});
            skArc(sketch, "E106", {"start": v(-79.5, 124.31) * mm, "mid": v(-82.4, 122.83) * mm, "end": v(-82.68, 119.59) * mm});
            skArc(sketch, "E107", {"start": v(-82.68, 119.59) * mm, "mid": v(-80.08, 118.3) * mm, "end": v(-77.48, 119.59) * mm});
            skArc(sketch, "E108", {"start": v(-77.48, 119.59) * mm, "mid": v(-78.5, 121.87) * mm, "end": v(-80.99, 121.56) * mm});
            skArc(sketch, "E109", {"start": v(-79.54, 123.65) * mm, "mid": v(-82.2, 120.5) * mm, "end": v(-78.18, 119.59) * mm});
            skArc(sketch, "E110", {"start": v(-78.18, 119.59) * mm, "mid": v(-79, 121.13) * mm, "end": v(-80.73, 120.81) * mm});
            skLineSegment(sketch, "E111", {"start": v(-79.5, 124.31) * mm, "end": v(-79.54, 123.65) * mm});
            skLineSegment(sketch, "E112", {"start": v(-80.99, 121.56) * mm, "end": v(-80.73, 120.81) * mm});
            skSolve(sketch);
        }
        {
            var Q0;
            Q0=qSketchRegion(id+"F22",true);
            var Q1;
            Q1=qConstructionFilter(qBodyType(qCreatedBy(id+"F22",EDGE),BodyType.WIRE),ConstructionObject.NO);
            extrude(context, id + "F23", {"entities" : qUnion([Q0]), "operationType" : NewBodyOperationType.REMOVE, "surfaceEntities" : qUnion([Q1]), "oppositeDirection" : true, "depth" : 25.4 * mm, "offsetDistance" : 25.4 * mm});
        }
        {
            var Q0;
            Q0=makeQuery(id+"F5.opExtrude","CAP_FACE",FACE,{"disambiguationData":[OSD([sQuery(id+"F4.wireOp",EDGE,"E36.bottom"),sQuery(id+"F4.wireOp",EDGE,"E36.top"),sQuery(id+"F4.wireOp",EDGE,"E36.left"),sQuery(id+"F4.wireOp",EDGE,"E36.right")])],"isStart":false});
            var sketch = newSketch(context, id + "F24", { "sketchPlane" : qUnion([Q0])});
            skArc(sketch, "E113", {"start": v(-68.48, 4.16) * mm, "mid": v(-71.6, 2.39) * mm, "end": v(-71.4, -1.2) * mm});
            skArc(sketch, "E114", {"start": v(-71.4, -1.2) * mm, "mid": v(-69.05, -2.1) * mm, "end": v(-66.7, -1.2) * mm});
            skArc(sketch, "E115", {"start": v(-66.7, -1.2) * mm, "mid": v(-67.23, 1.47) * mm, "end": v(-69.95, 1.35) * mm});
            skArc(sketch, "E116", {"start": v(-68.52, 3.4) * mm, "mid": v(-71.26, 0.83) * mm, "end": v(-68.1, -1.2) * mm});
            skArc(sketch, "E117", {"start": v(-68.1, -1.2) * mm, "mid": v(-68, 0.32) * mm, "end": v(-69.5, 0) * mm});
            skLineSegment(sketch, "E118", {"start": v(-68.48, 4.16) * mm, "end": v(-68.52, 3.4) * mm});
            skLineSegment(sketch, "E119", {"start": v(-69.95, 1.35) * mm, "end": v(-69.5, 0) * mm});
            skCircle(sketch, "E120", {"center": v(-57.9, 21.38) * mm, "radius": 1.59 * mm});
            skLineSegment(sketch, "E121", {"start": v(-57.9, 22.97) * mm, "end": v(-57.9, 28.84) * mm, "construction": true});
            skLineSegment(sketch, "E122", {"start": v(-57.9, 21.38) * mm, "end": v(-36.13, 21.38) * mm, "construction": true});
            skLineSegment(sketch, "E123", {"start": v(-57.9, 21.38) * mm, "end": v(-57.9, -26.98) * mm, "construction": true});
            skLineSegment(sketch, "E124", {"start": v(-57.9, 28.84) * mm, "end": v(-61.05, 28.84) * mm, "construction": true});
            skLineSegment(sketch, "E125", {"start": v(-57.9, 28.84) * mm, "end": v(-54.75, 28.84) * mm, "construction": true});
            skCircle(sketch, "E126", {"center": v(-53.2, 28.84) * mm, "radius": 1.56 * mm});
            skCircle(sketch, "E127", {"center": v(-62.61, 28.84) * mm, "radius": 1.56 * mm});
            skSolve(sketch);
        }
        {
            var Q0;
            Q0=qSketchRegion(id+"F24",true);
            extrude(context, id + "F25", {"entities" : qUnion([Q0]), "operationType" : NewBodyOperationType.REMOVE, "oppositeDirection" : true, "depth" : 25.4 * mm, "offsetDistance" : 25.4 * mm});
        }
        {
            var Q0;
            Q0=makeQuery(id+"F15.opPattern","COPY",FACE,{"derivedFrom":makeQuery(id+"F5.opExtrude","CAP_FACE",FACE,{"disambiguationData":[OSD([sQuery(id+"F4.wireOp",EDGE,"E36.bottom"),sQuery(id+"F4.wireOp",EDGE,"E36.top"),sQuery(id+"F4.wireOp",EDGE,"E36.left"),sQuery(id+"F4.wireOp",EDGE,"E36.right")])],"isStart":true}),"instanceName":"1"});
            var sketch = newSketch(context, id + "F26", { "sketchPlane" : qUnion([Q0])});
            skArc(sketch, "E128", {"start": v(-87.7, -20.93) * mm, "mid": v(-90.74, -22.48) * mm, "end": v(-91.02, -25.86) * mm});
            skArc(sketch, "E129", {"start": v(-91.02, -25.86) * mm, "mid": v(-88.3, -27.2) * mm, "end": v(-85.6, -25.86) * mm});
            skArc(sketch, "E130", {"start": v(-85.6, -25.86) * mm, "mid": v(-86.67, -23.48) * mm, "end": v(-89.26, -23.8) * mm});
            skArc(sketch, "E131", {"start": v(-87.74, -21.62) * mm, "mid": v(-90.52, -24.91) * mm, "end": v(-86.32, -25.86) * mm});
            skArc(sketch, "E132", {"start": v(-86.32, -25.86) * mm, "mid": v(-87.19, -24.25) * mm, "end": v(-88.99, -24.58) * mm});
            skLineSegment(sketch, "E133", {"start": v(-87.7, -20.93) * mm, "end": v(-87.74, -21.62) * mm});
            skLineSegment(sketch, "E134", {"start": v(-89.26, -23.8) * mm, "end": v(-88.99, -24.58) * mm});
            skLineSegment(sketch, "E135", {"start": v(-103.64, -60.66) * mm, "end": v(-103.64, -35.26) * mm, "construction": true});
            skCircle(sketch, "E136", {"center": v(-103.64, -35.26) * mm, "radius": 1.59 * mm});
            skLineSegment(sketch, "E137", {"start": v(-103.64, -36.85) * mm, "end": v(-103.64, -42.71) * mm, "construction": true});
            skLineSegment(sketch, "E138", {"start": v(-103.64, -42.71) * mm, "end": v(-100.5, -42.71) * mm, "construction": true});
            skLineSegment(sketch, "E139", {"start": v(-103.64, -42.71) * mm, "end": v(-106.8, -42.71) * mm, "construction": true});
            skCircle(sketch, "E140", {"center": v(-108.35, -42.71) * mm, "radius": 1.56 * mm});
            skCircle(sketch, "E141", {"center": v(-98.93, -42.71) * mm, "radius": 1.56 * mm});
            skSolve(sketch);
        }
        {
            var Q0;
            Q0=qSketchRegion(id+"F26",true);
            extrude(context, id + "F27", {"entities" : qUnion([Q0]), "operationType" : NewBodyOperationType.REMOVE, "oppositeDirection" : true, "depth" : 25.4 * mm, "offsetDistance" : 25.4 * mm});
        }
        {
            var Q0;
            Q0=makeQuery(id+"F5.opExtrude","SWEPT_BODY",BODY,{"disambiguationData":[OSD([sQuery(id+"F4.wireOp",EDGE,"E36.bottom"),sQuery(id+"F4.wireOp",EDGE,"E36.top"),sQuery(id+"F4.wireOp",EDGE,"E36.left"),sQuery(id+"F4.wireOp",EDGE,"E36.right")])]});
            var Q1;
            Q1=makeQuery(id+"F9.opExtrude","SWEPT_BODY",BODY,{"disambiguationData":[OSD([sQuery(id+"F8.wireOp",EDGE,"E63.bottom"),sQuery(id+"F8.wireOp",EDGE,"E63.top"),sQuery(id+"F8.wireOp",EDGE,"E63.left"),sQuery(id+"F8.wireOp",EDGE,"E63.right")])]});
            transform(context, id + "F28", {"entities" : qUnion([Q0, Q1]), "transformType" : TransformType.TRANSLATION_3D, "dx" : -50.8 * mm, "dy" : 0 * mm, "dz" : 0 * mm, "makeCopy" : false});
        }
        {
            var Q0;
            Q0=makeQuery(id+"F9.opExtrude","SWEPT_BODY",BODY,{"disambiguationData":[OSD([sQuery(id+"F8.wireOp",EDGE,"E63.bottom"),sQuery(id+"F8.wireOp",EDGE,"E63.top"),sQuery(id+"F8.wireOp",EDGE,"E63.left"),sQuery(id+"F8.wireOp",EDGE,"E63.right")])]});
            transform(context, id + "F29", {"entities" : qUnion([Q0]), "transformType" : TransformType.TRANSLATION_3D, "dx" : 38.1 * mm, "dy" : 50.8 * mm, "dz" : 0 * mm, "makeCopy" : false});
        }
    });
